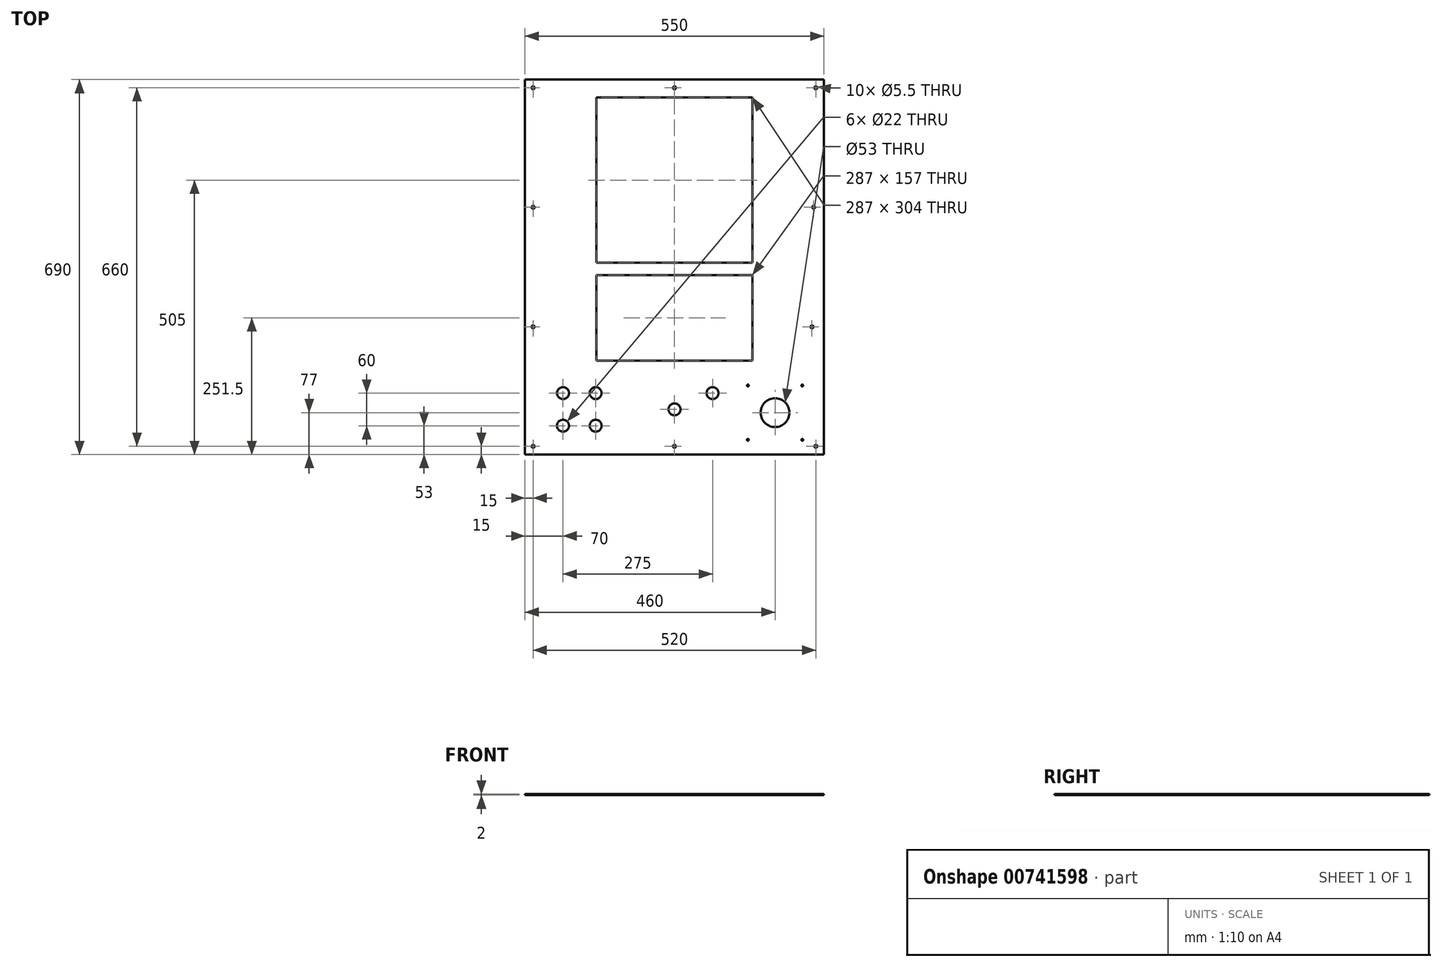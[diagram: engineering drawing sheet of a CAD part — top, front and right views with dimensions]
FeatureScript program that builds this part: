
annotation { "Feature Type Name" : "Feature", "Feature Type Description" : "" }
export const myFeature = defineFeature(function(context is Context, id is Id, definition is map)
    precondition{}
    {
        {
            var Q0;
            Q0=qCreatedBy(makeId("Top.planeOp"),FACE);
            var sketch = newSketch(context, id + "F0", { "sketchPlane" : qUnion([Q0])});
            skLineSegment(sketch, "E0.bottom", {"start": v(275, 345) * mm, "end": v(-275, 345) * mm});
            skLineSegment(sketch, "E0.top", {"start": v(275, -345) * mm, "end": v(-275, -345) * mm});
            skLineSegment(sketch, "E0.left", {"start": v(275, 345) * mm, "end": v(275, -345) * mm});
            skLineSegment(sketch, "E0.right", {"start": v(-275, 345) * mm, "end": v(-275, -345) * mm});
            skPoint(sketch, "E0.middle", {"position": v(0, 0) * mm});
            skLineSegment(sketch, "E1.bottom", {"start": v(143.5, 312) * mm, "end": v(-143.5, 312) * mm});
            skLineSegment(sketch, "E1.top", {"start": v(143.5, 8) * mm, "end": v(-143.5, 8) * mm});
            skLineSegment(sketch, "E1.left", {"start": v(143.5, 312) * mm, "end": v(143.5, 8) * mm});
            skLineSegment(sketch, "E1.right", {"start": v(-143.5, 312) * mm, "end": v(-143.5, 8) * mm});
            skPoint(sketch, "E1.middle", {"position": v(0, 160) * mm});
            skLineSegment(sketch, "E2.bottom", {"start": v(143.5, -172) * mm, "end": v(-143.5, -172) * mm});
            skLineSegment(sketch, "E2.top", {"start": v(143.5, -15) * mm, "end": v(-143.5, -15) * mm});
            skLineSegment(sketch, "E2.left", {"start": v(143.5, -172) * mm, "end": v(143.5, -15) * mm});
            skLineSegment(sketch, "E2.right", {"start": v(-143.5, -172) * mm, "end": v(-143.5, -15) * mm});
            skPoint(sketch, "E2.middle", {"position": v(0, -93.5) * mm});
            skSolve(sketch);
        }
        {
            var Q0;
            Q0=makeQuery(id+"F0.imprint","IMPRINT",FACE,{"disambiguationData":[TD([[makeQuery(id+"F0.imprint","IMPRINT",EDGE,{"derivedFrom":sQuery(id+"F0.wireOp",EDGE,"E0.bottom")}),1.0]])]});
            extrude(context, id + "F1", {"entities" : qUnion([Q0]), "depth" : 2 * mm, "offsetDistance" : 25 * mm});
        }
        {
            var Q0;
            Q0=makeQuery(id+"F1.opExtrude","CAP_FACE",FACE,{"disambiguationData":[OSD([sQuery(id+"F0.wireOp",EDGE,"E0.bottom"),sQuery(id+"F0.wireOp",EDGE,"E0.top"),sQuery(id+"F0.wireOp",EDGE,"E0.left"),sQuery(id+"F0.wireOp",EDGE,"E0.right"),sQuery(id+"F0.wireOp",EDGE,"E1.bottom"),sQuery(id+"F0.wireOp",EDGE,"E1.top"),sQuery(id+"F0.wireOp",EDGE,"E1.left"),sQuery(id+"F0.wireOp",EDGE,"E1.right"),sQuery(id+"F0.wireOp",EDGE,"E2.bottom"),sQuery(id+"F0.wireOp",EDGE,"E2.top"),sQuery(id+"F0.wireOp",EDGE,"E2.left"),sQuery(id+"F0.wireOp",EDGE,"E2.right")])],"isStart":false});
            var sketch = newSketch(context, id + "F2", { "sketchPlane" : qUnion([Q0])});
            skPoint(sketch, "E3.middle", {"position": v(185, -268) * mm});
            skCircle(sketch, "E4", {"center": v(185, -268) * mm, "radius": 26.5 * mm});
            skPoint(sketch, "E5", {"position": v(235, -218) * mm});
            skPoint(sketch, "E6", {"position": v(235, -318) * mm});
            skPoint(sketch, "E7", {"position": v(135, -318) * mm});
            skPoint(sketch, "E8", {"position": v(135, -218) * mm});
            skSolve(sketch);
        }
        {
            var Q0;
            Q0 = qSketchRegion(id + "F2", true);
            extrude(context, id + "F3", {"entities" : qUnion([Q0]), "operationType" : NewBodyOperationType.REMOVE, "endBound" : BoundingType.THROUGH_ALL, "oppositeDirection" : true, "depth" : 25 * mm, "offsetDistance" : 25 * mm});
        }
        {
            var Q0;
            Q0=makeQuery(id+"F1.opExtrude","CAP_FACE",FACE,{"disambiguationData":[OSD([sQuery(id+"F0.wireOp",EDGE,"E0.bottom"),sQuery(id+"F0.wireOp",EDGE,"E0.top"),sQuery(id+"F0.wireOp",EDGE,"E0.left"),sQuery(id+"F0.wireOp",EDGE,"E0.right"),sQuery(id+"F0.wireOp",EDGE,"E1.bottom"),sQuery(id+"F0.wireOp",EDGE,"E1.top"),sQuery(id+"F0.wireOp",EDGE,"E1.left"),sQuery(id+"F0.wireOp",EDGE,"E1.right"),sQuery(id+"F0.wireOp",EDGE,"E2.bottom"),sQuery(id+"F0.wireOp",EDGE,"E2.top"),sQuery(id+"F0.wireOp",EDGE,"E2.left"),sQuery(id+"F0.wireOp",EDGE,"E2.right")])],"isStart":false});
            var sketch = newSketch(context, id + "F4", { "sketchPlane" : qUnion([Q0])});
            skPoint(sketch, "E9", {"position": v(235, -218) * mm});
            skPoint(sketch, "E10", {"position": v(235, -318) * mm});
            skPoint(sketch, "E11", {"position": v(135, -318) * mm});
            skPoint(sketch, "E12", {"position": v(135, -218) * mm});
            skPoint(sketch, "E13", {"position": v(185, -268) * mm});
            skSolve(sketch);
        }
        {
            var Q0;
            Q0=sQuery(id+"F4.wireOp",VERTEX,"E12");
            var Q1;
            Q1=sQuery(id+"F4.wireOp",VERTEX,"E9");
            var Q2;
            Q2=sQuery(id+"F4.wireOp",VERTEX,"E10");
            var Q3;
            Q3=sQuery(id+"F4.wireOp",VERTEX,"E11");
            var Q4;
            Q4=makeQuery(id+"F1.opExtrude","SWEPT_BODY",BODY,{"disambiguationData":[OSD([sQuery(id+"F0.wireOp",EDGE,"E0.bottom"),sQuery(id+"F0.wireOp",EDGE,"E0.top"),sQuery(id+"F0.wireOp",EDGE,"E0.left"),sQuery(id+"F0.wireOp",EDGE,"E0.right"),sQuery(id+"F0.wireOp",EDGE,"E1.bottom"),sQuery(id+"F0.wireOp",EDGE,"E1.top"),sQuery(id+"F0.wireOp",EDGE,"E1.left"),sQuery(id+"F0.wireOp",EDGE,"E1.right"),sQuery(id+"F0.wireOp",EDGE,"E2.bottom"),sQuery(id+"F0.wireOp",EDGE,"E2.top"),sQuery(id+"F0.wireOp",EDGE,"E2.left"),sQuery(id+"F0.wireOp",EDGE,"E2.right")])]});
            hole(context, id + "F5", {"style" : HoleStyle.SIMPLE, "endStyle" : HoleEndStyle.THROUGH, "standardTappedOrClearance" : lookupTablePath({ "standard" : "ISO", "engagement" : "75%", "pitch" : "0.7 mm", "size" : "M4", "type" : "Tapped" }), "standardBlindInLast" : lookupTablePath({ "standard" : "ISO", "engagement" : "75%", "pitch" : "0.7 mm", "size" : "M4", "type" : "Tapped" }), "holeDiameter" : 3.3 * mm, "majorDiameter" : 4 * mm, "showTappedDepth" : true, "isTappedThrough" : true, "tappedDepth" : 8 * mm, "tapClearance" : 3, "locations" : qUnion([Q0, Q1, Q2, Q3]), "scope" : qUnion([Q4])});
        }
        {
            var Q0;
            Q0=makeQuery(id+"F1.opExtrude","CAP_FACE",FACE,{"disambiguationData":[OSD([sQuery(id+"F0.wireOp",EDGE,"E0.bottom"),sQuery(id+"F0.wireOp",EDGE,"E0.top"),sQuery(id+"F0.wireOp",EDGE,"E0.left"),sQuery(id+"F0.wireOp",EDGE,"E0.right"),sQuery(id+"F0.wireOp",EDGE,"E1.bottom"),sQuery(id+"F0.wireOp",EDGE,"E1.top"),sQuery(id+"F0.wireOp",EDGE,"E1.left"),sQuery(id+"F0.wireOp",EDGE,"E1.right"),sQuery(id+"F0.wireOp",EDGE,"E2.bottom"),sQuery(id+"F0.wireOp",EDGE,"E2.top"),sQuery(id+"F0.wireOp",EDGE,"E2.left"),sQuery(id+"F0.wireOp",EDGE,"E2.right")])],"isStart":false});
            var sketch = newSketch(context, id + "F6", { "sketchPlane" : qUnion([Q0])});
            skPoint(sketch, "E14", {"position": v(185, -268) * mm});
            skPoint(sketch, "E15", {"position": v(-205, -232) * mm});
            skPoint(sketch, "E16", {"position": v(-145, -232) * mm});
            skPoint(sketch, "E17", {"position": v(0, -262) * mm});
            skPoint(sketch, "E18", {"position": v(70, -232) * mm});
            skPoint(sketch, "E19.middle.positionSnap0", {"position": v(0, -172) * mm});
            skPoint(sketch, "E19.cornerSnap0", {"position": v(0, -172) * mm});
            skPoint(sketch, "E19.centerSnap0", {"position": v(0, -172) * mm});
            skPoint(sketch, "E20", {"position": v(-205, -292) * mm});
            skPoint(sketch, "E21", {"position": v(-145, -292) * mm});
            skSolve(sketch);
        }
        {
            var Q0;
            Q0=sQuery(id+"F6.wireOp",VERTEX,"E15");
            var Q1;
            Q1=sQuery(id+"F6.wireOp",VERTEX,"E16");
            var Q2;
            Q2=sQuery(id+"F6.wireOp",VERTEX,"E17");
            var Q3;
            Q3=sQuery(id+"F6.wireOp",VERTEX,"E18");
            var Q4;
            Q4=sQuery(id+"F6.wireOp",VERTEX,"E20");
            var Q5;
            Q5=sQuery(id+"F6.wireOp",VERTEX,"E21");
            var Q6;
            Q6=makeQuery(id+"F1.opExtrude","SWEPT_BODY",BODY,{"disambiguationData":[OSD([sQuery(id+"F0.wireOp",EDGE,"E0.bottom"),sQuery(id+"F0.wireOp",EDGE,"E0.top"),sQuery(id+"F0.wireOp",EDGE,"E0.left"),sQuery(id+"F0.wireOp",EDGE,"E0.right"),sQuery(id+"F0.wireOp",EDGE,"E1.bottom"),sQuery(id+"F0.wireOp",EDGE,"E1.top"),sQuery(id+"F0.wireOp",EDGE,"E1.left"),sQuery(id+"F0.wireOp",EDGE,"E1.right"),sQuery(id+"F0.wireOp",EDGE,"E2.bottom"),sQuery(id+"F0.wireOp",EDGE,"E2.top"),sQuery(id+"F0.wireOp",EDGE,"E2.left"),sQuery(id+"F0.wireOp",EDGE,"E2.right")])]});
            hole(context, id + "F7", {"style" : HoleStyle.SIMPLE, "endStyle" : HoleEndStyle.THROUGH, "holeDiameter" : 22 * mm, "majorDiameter" : 4 * mm, "isTappedThrough" : true, "tappedDepth" : 8 * mm, "tapClearance" : 3, "locations" : qUnion([Q0, Q1, Q2, Q3, Q4, Q5]), "scope" : qUnion([Q6])});
        }
        {
            var Q0;
            Q0=makeQuery(id+"F1.opExtrude","CAP_FACE",FACE,{"disambiguationData":[OSD([sQuery(id+"F0.wireOp",EDGE,"E0.bottom"),sQuery(id+"F0.wireOp",EDGE,"E0.top"),sQuery(id+"F0.wireOp",EDGE,"E0.left"),sQuery(id+"F0.wireOp",EDGE,"E0.right"),sQuery(id+"F0.wireOp",EDGE,"E1.bottom"),sQuery(id+"F0.wireOp",EDGE,"E1.top"),sQuery(id+"F0.wireOp",EDGE,"E1.left"),sQuery(id+"F0.wireOp",EDGE,"E1.right"),sQuery(id+"F0.wireOp",EDGE,"E2.bottom"),sQuery(id+"F0.wireOp",EDGE,"E2.top"),sQuery(id+"F0.wireOp",EDGE,"E2.left"),sQuery(id+"F0.wireOp",EDGE,"E2.right")])],"isStart":false});
            var sketch = newSketch(context, id + "F8", { "sketchPlane" : qUnion([Q0])});
            skCircle(sketch, "E22", {"center": v(0, -262) * mm, "radius": 30.1 * mm});
            skLineSegment(sketch, "E23.bottom", {"start": v(125, -208) * mm, "end": v(245, -208) * mm});
            skLineSegment(sketch, "E23.top", {"start": v(125, -328) * mm, "end": v(245, -328) * mm});
            skLineSegment(sketch, "E23.left", {"start": v(125, -208) * mm, "end": v(125, -328) * mm});
            skLineSegment(sketch, "E23.right", {"start": v(245, -208) * mm, "end": v(245, -328) * mm});
            skPoint(sketch, "E23.middle", {"position": v(185, -268) * mm});
            skSolve(sketch);
        }
        {
            var Q0;
            Q0=makeQuery(id+"F8.imprint","IMPRINT",FACE,{"disambiguationData":[TD([[makeQuery(id+"F8.imprint","IMPRINT",EDGE,{"derivedFrom":sQuery(id+"F8.wireOp",EDGE,"E22")}),-1.0]])]});
            var sketch = newSketch(context, id + "F9", { "sketchPlane" : qUnion([Q0])});
            skPoint(sketch, "E24", {"position": v(-260, 330) * mm});
            skPoint(sketch, "E25", {"position": v(0, 330) * mm});
            skPoint(sketch, "E26", {"position": v(260, 330) * mm});
            skPoint(sketch, "E27", {"position": v(-260, -330) * mm});
            skPoint(sketch, "E28", {"position": v(0, -330) * mm});
            skPoint(sketch, "E29", {"position": v(260, -330) * mm});
            skPoint(sketch, "E30", {"position": v(-260, 110) * mm});
            skPoint(sketch, "E31", {"position": v(-260, -110) * mm});
            skPoint(sketch, "E32", {"position": v(255.99, 110) * mm});
            skPoint(sketch, "E33", {"position": v(252.9, -110) * mm});
            skSolve(sketch);
        }
        {
            var Q0;
            Q0=sQuery(id+"F9.wireOp",VERTEX,"E24");
            var Q1;
            Q1=sQuery(id+"F9.wireOp",VERTEX,"E25");
            var Q2;
            Q2=sQuery(id+"F9.wireOp",VERTEX,"E26");
            var Q3;
            Q3=sQuery(id+"F9.wireOp",VERTEX,"E32");
            var Q4;
            Q4=sQuery(id+"F9.wireOp",VERTEX,"E33");
            var Q5;
            Q5=sQuery(id+"F9.wireOp",VERTEX,"E29");
            var Q6;
            Q6=sQuery(id+"F9.wireOp",VERTEX,"E28");
            var Q7;
            Q7=sQuery(id+"F9.wireOp",VERTEX,"E27");
            var Q8;
            Q8=sQuery(id+"F9.wireOp",VERTEX,"E31");
            var Q9;
            Q9=sQuery(id+"F9.wireOp",VERTEX,"E30");
            var Q10;
            Q10=makeQuery(id+"F1.opExtrude","SWEPT_BODY",BODY,{"disambiguationData":[OSD([sQuery(id+"F0.wireOp",EDGE,"E0.bottom"),sQuery(id+"F0.wireOp",EDGE,"E0.top"),sQuery(id+"F0.wireOp",EDGE,"E0.left"),sQuery(id+"F0.wireOp",EDGE,"E0.right"),sQuery(id+"F0.wireOp",EDGE,"E1.bottom"),sQuery(id+"F0.wireOp",EDGE,"E1.top"),sQuery(id+"F0.wireOp",EDGE,"E1.left"),sQuery(id+"F0.wireOp",EDGE,"E1.right"),sQuery(id+"F0.wireOp",EDGE,"E2.bottom"),sQuery(id+"F0.wireOp",EDGE,"E2.top"),sQuery(id+"F0.wireOp",EDGE,"E2.left"),sQuery(id+"F0.wireOp",EDGE,"E2.right")])]});
            hole(context, id + "F10", {"style" : HoleStyle.SIMPLE, "endStyle" : HoleEndStyle.THROUGH, "holeDiameter" : 5.5 * mm, "majorDiameter" : 5 * mm, "isTappedThrough" : true, "tappedDepth" : 8 * mm, "tapClearance" : 3, "locations" : qUnion([Q0, Q1, Q2, Q3, Q4, Q5, Q6, Q7, Q8, Q9]), "scope" : qUnion([Q10])});
        }
    });
